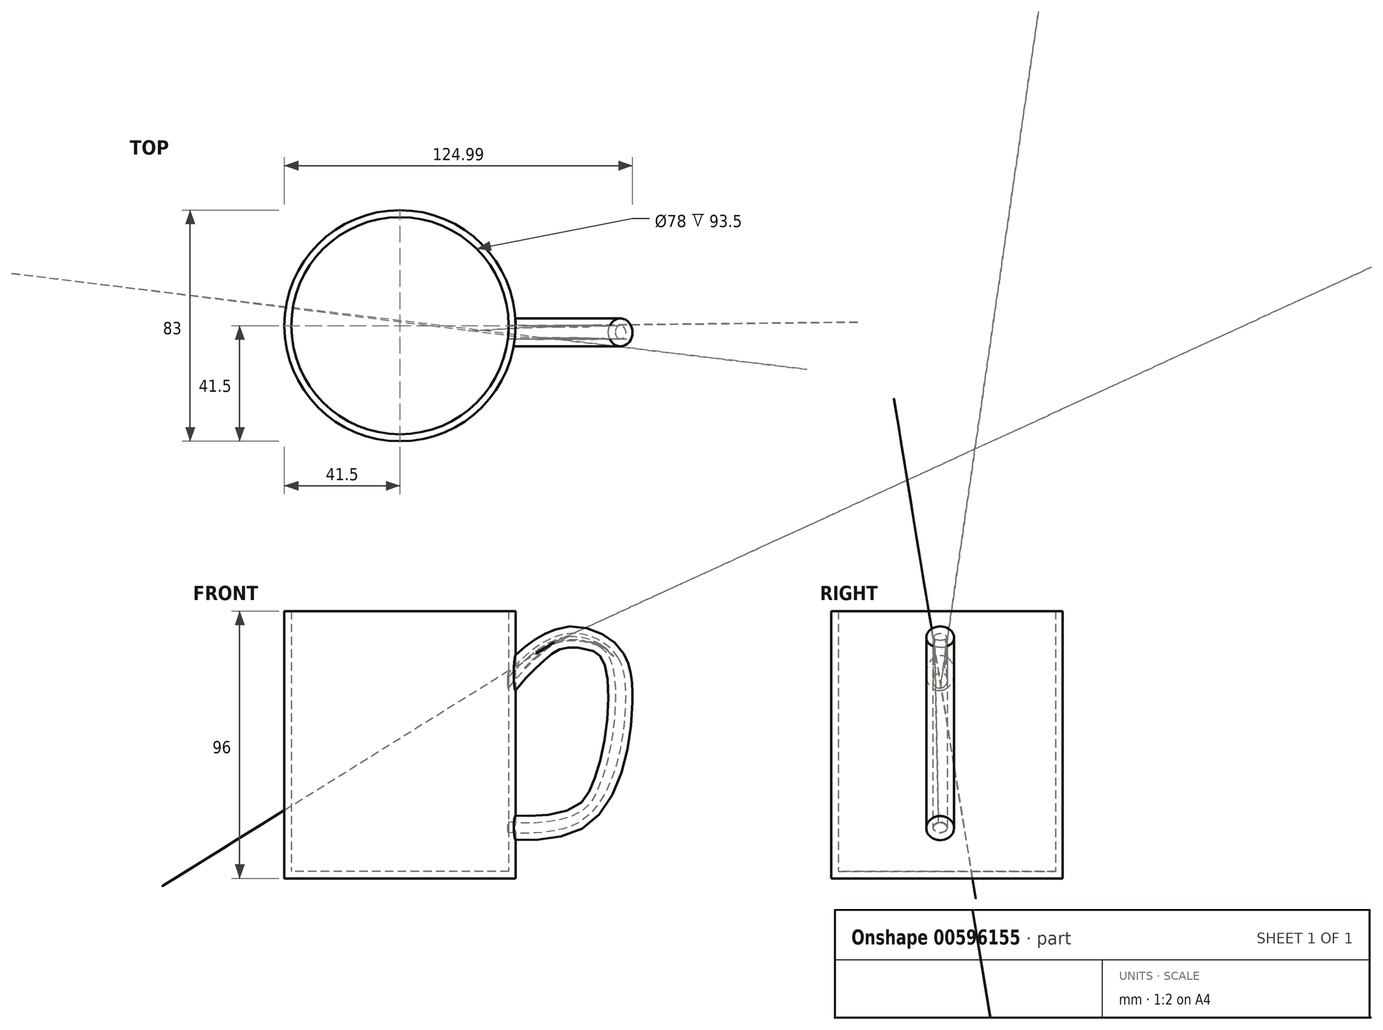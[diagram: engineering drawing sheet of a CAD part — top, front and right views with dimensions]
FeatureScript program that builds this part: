
annotation { "Feature Type Name" : "Feature", "Feature Type Description" : "" }
export const myFeature = defineFeature(function(context is Context, id is Id, definition is map)
    precondition{}
    {
        {
            var Q0;
            Q0=qCreatedBy(makeId("Top.planeOp"),FACE);
            var sketch = newSketch(context, id + "F0", { "sketchPlane" : qUnion([Q0])});
            skCircle(sketch, "E0", {"center": v(0, 0) * mm, "radius": 41.5 * mm});
            skSolve(sketch);
        }
        {
            var Q0;
            Q0 = qSketchRegion(id + "F0", true);
            extrude(context, id + "F1", {"entities" : qUnion([Q0]), "depth" : 96 * mm, "offsetDistance" : 25 * mm});
        }
        {
            var Q0;
            Q0=qCreatedBy(makeId("Front.planeOp"),FACE);
            var sketch = newSketch(context, id + "F2", { "sketchPlane" : qUnion([Q0])});
            skFitSpline(sketch, "E1", {"points": [v(31.93, 75.15) * mm, v(59.84, 93.99) * mm, v(80.99, 85.83) * mm, v(87.1, 61.63) * mm, v(67.3, 14.78) * mm, v(31.05, 11.01) * mm], "startDerivative": vector(121.25, 151.15) * mm, "endDerivative": vector(-56.26, 6.2) * mm});
            skSolve(sketch);
        }
        {
            var Q0;
            Q0=qCreatedBy(makeId("Right.planeOp"),FACE);
            cPlane(context, id + "F3", {"entities" : qUnion([Q0]), "cplaneType" : CPlaneType.OFFSET, "offset" : 50 * mm, "width" : 150 * mm, "height" : 150 * mm});
        }
        {
            var Q0;
            Q0=qCreatedBy(id+"F3.planeOp",FACE);
            var sketch = newSketch(context, id + "F4", { "sketchPlane" : qUnion([Q0])});
            skCircle(sketch, "E2", {"center": v(-2.39, 81.73) * mm, "radius": 5 * mm});
            skSolve(sketch);
        }
        {
            var Q0;
            Q0=makeQuery(id+"F4.imprint","IMPRINT",FACE,{"disambiguationData":[TD([[makeQuery(id+"F4.imprint","IMPRINT",EDGE,{"derivedFrom":sQuery(id+"F4.wireOp",EDGE,"E2")}),1.0]])]});
            var Q1;
            Q1=sQuery(id+"F2.wireOp",EDGE,"E1");
            sweep(context, id + "F5", {"operationType" : NewBodyOperationType.ADD, "profiles" : qUnion([Q0]), "path" : qUnion([Q1])});
        }
        {
            var Q0;
            Q0=makeQuery(id+"F1.opExtrude","CAP_FACE",FACE,{"disambiguationData":[OSD([sQuery(id+"F0.wireOp",EDGE,"E0")])],"isStart":false});
            shell(context, id + "F6", {"entities" : qUnion([Q0]), "thickness" : 2.5 * mm});
        }
    });
